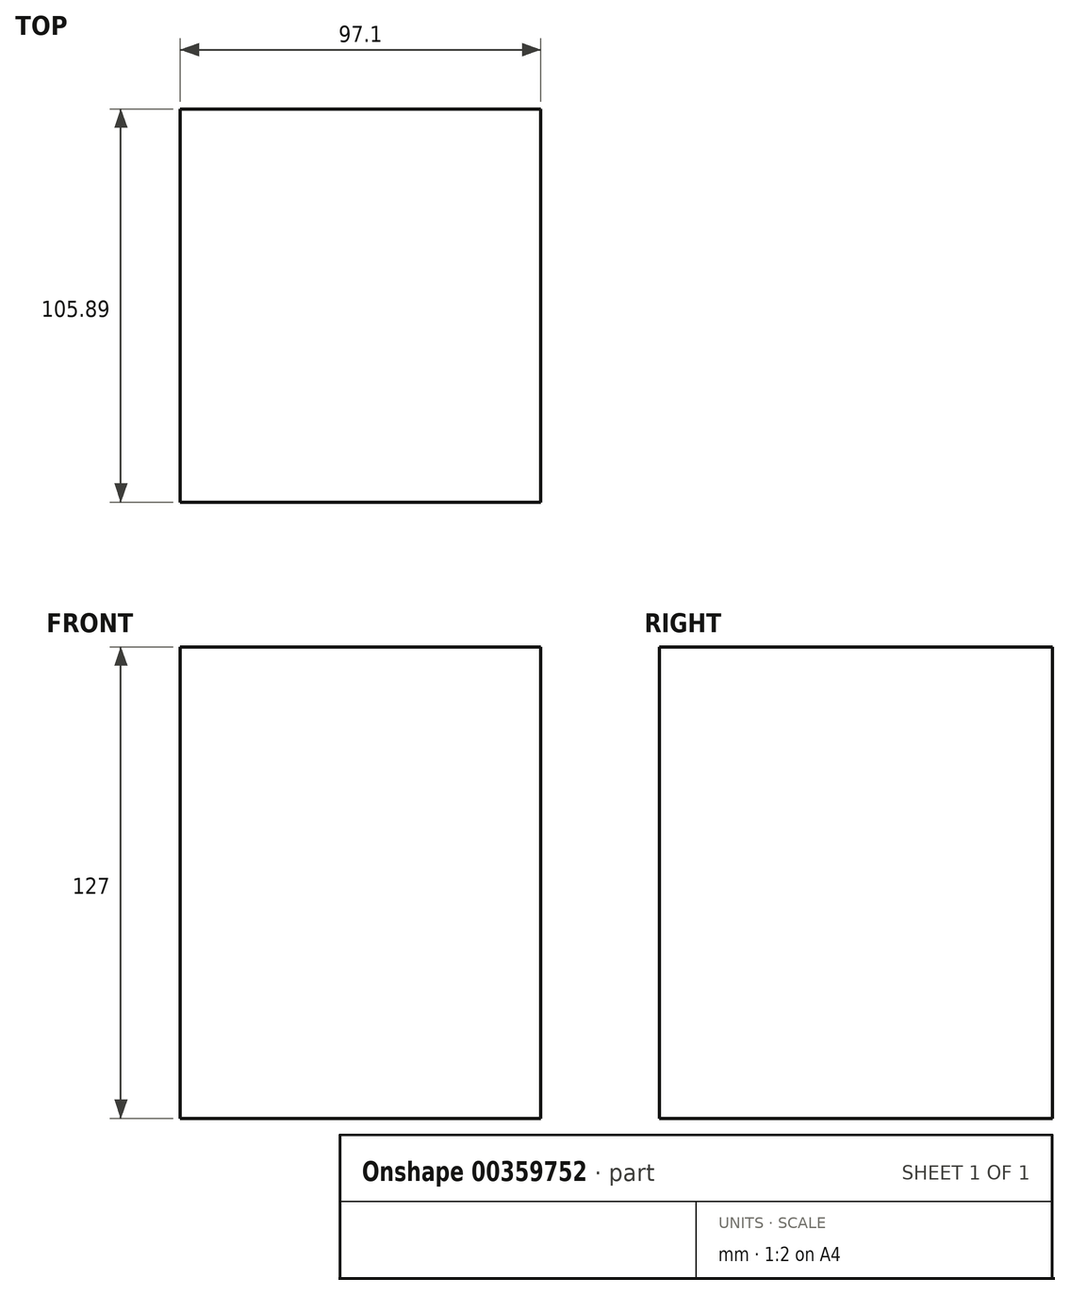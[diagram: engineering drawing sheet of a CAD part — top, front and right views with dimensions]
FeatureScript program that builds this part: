
annotation { "Feature Type Name" : "Feature", "Feature Type Description" : "" }
export const myFeature = defineFeature(function(context is Context, id is Id, definition is map)
    precondition{}
    {
        {
            var Q0;
            Q0=qCreatedBy(makeId("Top.planeOp"),FACE);
            var sketch = newSketch(context, id + "F0", { "sketchPlane" : qUnion([Q0])});
            skLineSegment(sketch, "E0.bottom", {"start": v(53.8, 58.42) * mm, "end": v(-43.3, 58.42) * mm});
            skLineSegment(sketch, "E0.top", {"start": v(53.8, -47.47) * mm, "end": v(-43.3, -47.47) * mm});
            skLineSegment(sketch, "E0.left", {"start": v(53.8, 58.42) * mm, "end": v(53.8, -47.47) * mm});
            skLineSegment(sketch, "E0.right", {"start": v(-43.3, 58.42) * mm, "end": v(-43.3, -47.47) * mm});
            skSolve(sketch);
        }
        {
            var Q0;
            Q0=makeQuery(id+"F0.imprint","IMPRINT",FACE,{"disambiguationData":[TD([[makeQuery(id+"F0.imprint","IMPRINT",EDGE,{"derivedFrom":sQuery(id+"F0.wireOp",EDGE,"E0.bottom")}),1.0]])]});
            extrude(context, id + "F1", {"entities" : qUnion([Q0]), "depth" : 50.8 * mm});
        }
        {
            var Q0;
            Q0=makeQuery(id+"F1.opExtrude","CAP_FACE",FACE,{"disambiguationData":[OSD([sQuery(id+"F0.wireOp",EDGE,"E0.bottom"),sQuery(id+"F0.wireOp",EDGE,"E0.top"),sQuery(id+"F0.wireOp",EDGE,"E0.left"),sQuery(id+"F0.wireOp",EDGE,"E0.right")])],"isStart":false});
            var sketch = newSketch(context, id + "F2", { "sketchPlane" : qUnion([Q0])});
            skSolve(sketch);
        }
        {
            var Q0;
            Q0=makeQuery(id+"F2.imprint","IMPRINT",FACE,{"disambiguationData":[TD([[makeQuery(id+"F2.imprint","IMPRINT",EDGE,{"derivedFrom":makeQuery(id+"F1.opExtrude","CAP_EDGE",EDGE,{"disambiguationData":[OSD([sQuery(id+"F0.wireOp",EDGE,"E0.bottom")])],"isStart":false})}),1.0]])]});
            extrude(context, id + "F3", {"entities" : qUnion([Q0]), "operationType" : NewBodyOperationType.ADD, "depth" : 76.2 * mm});
        }
        {
            var Q0;
            {var subQ0=sQuery(id+"F0.wireOp",EDGE,"E0.top");Q0=makeQuery(id+"F3.boolean.opBoolean","MERGE",FACE,{"derivedFrom":[makeQuery(id+"F1.opExtrude","SWEPT_FACE",FACE,{"disambiguationData":[OSD([subQ0])]}),makeQuery(id+"F3.opExtrude","SWEPT_FACE",FACE,{"disambiguationData":[OSD([subQ0])]})]});}
            extrude(context, id + "F4", {"entities" : qUnion([Q0]), "operationType" : NewBodyOperationType.ADD, "depth" : -50.8 * mm});
        }
    });
